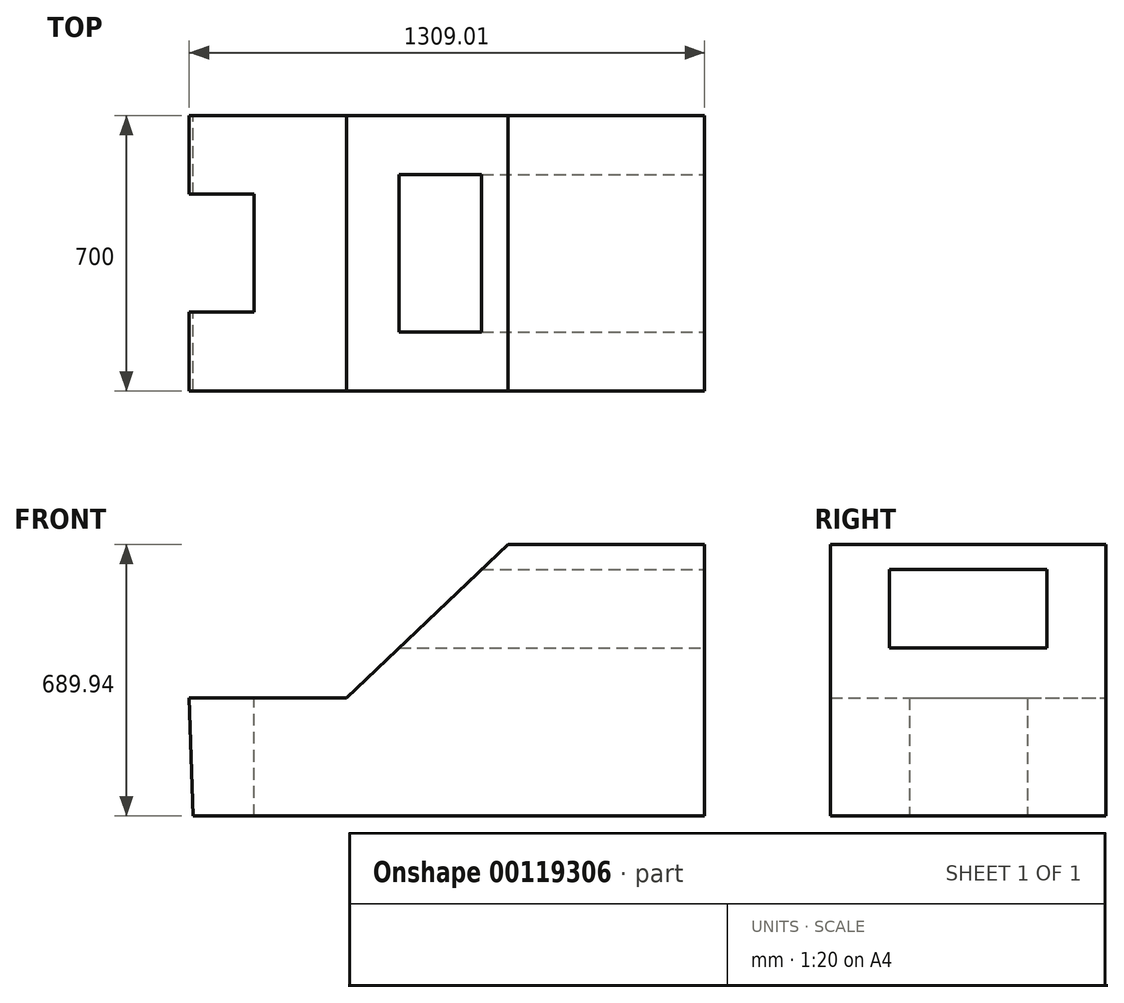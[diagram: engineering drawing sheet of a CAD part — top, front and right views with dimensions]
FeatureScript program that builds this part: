
annotation { "Feature Type Name" : "Feature", "Feature Type Description" : "" }
export const myFeature = defineFeature(function(context is Context, id is Id, definition is map)
    precondition{}
    {
        {
            var Q0;
            Q0=qCreatedBy(makeId("Front.planeOp"),FACE);
            var sketch = newSketch(context, id + "F0", { "sketchPlane" : qUnion([Q0])});
            skLineSegment(sketch, "E0.bottom", {"start": v(-800, -689.94) * mm, "end": v(500, -689.94) * mm});
            skLineSegment(sketch, "E0.left", {"start": v(-800, -689.94) * mm, "end": v(-809, -390.08) * mm});
            skPoint(sketch, "E0.middle", {"position": v(0, 0) * mm});
            skLineSegment(sketch, "E1", {"start": v(-809, -390.08) * mm, "end": v(-409, -390.08) * mm});
            skLineSegment(sketch, "E2", {"start": v(-409, -390.08) * mm, "end": v(0, 0) * mm});
            skLineSegment(sketch, "E3", {"start": v(500, 0) * mm, "end": v(500, -700) * mm});
            skLineSegment(sketch, "E4", {"start": v(-799.7, -700) * mm, "end": v(-800, -689.94) * mm});
            skPoint(sketch, "E5.start.orphan", {"position": v(25.9, 0) * mm});
            skLineSegment(sketch, "E6", {"start": v(0, 0) * mm, "end": v(500, 0) * mm});
            skPoint(sketch, "E7.start.orphan", {"position": v(-841.45, 689.94) * mm});
            skPoint(sketch, "E0.right.end.orphan", {"position": v(800, 689.94) * mm});
            skPoint(sketch, "E8.orphan", {"position": v(841.45, -689.94) * mm});
            skSolve(sketch);
        }
        {
            var Q0;
            Q0 = qSketchRegion(id + "F0", true);
            extrude(context, id + "F1", {"entities" : qUnion([Q0]), "depth" : 700 * mm});
        }
        {
            var Q0;
            Q0=makeQuery(id+"F1.opExtrude","SWEPT_FACE",FACE,{"disambiguationData":[OSD([sQuery(id+"F0.wireOp",EDGE,"E1")])]});
            var sketch = newSketch(context, id + "F2", { "sketchPlane" : qUnion([Q0])});
            skLineSegment(sketch, "E9.top", {"start": v(-644.94, -200) * mm, "end": v(-973.08, -200) * mm});
            skLineSegment(sketch, "E9.left", {"start": v(-644.94, -500) * mm, "end": v(-644.94, -200) * mm});
            skLineSegment(sketch, "E9.right", {"start": v(-973.08, -500) * mm, "end": v(-973.08, -200) * mm});
            skPoint(sketch, "E9.middle", {"position": v(-809, -350) * mm});
            skLineSegment(sketch, "E10", {"start": v(-644.94, -500) * mm, "end": v(-973.08, -500) * mm});
            skSolve(sketch);
        }
        {
            var Q0;
            Q0 = qSketchRegion(id + "F2", true);
            extrude(context, id + "F3", {"entities" : qUnion([Q0]), "operationType" : NewBodyOperationType.REMOVE, "endBound" : BoundingType.THROUGH_ALL, "oppositeDirection" : true, "depth" : 25 * mm});
        }
        {
            var Q0;
            Q0=makeQuery(id+"F1.opExtrude","SWEPT_FACE",FACE,{"disambiguationData":[OSD([sQuery(id+"F0.wireOp",EDGE,"E3")])]});
            var sketch = newSketch(context, id + "F4", { "sketchPlane" : qUnion([Q0])});
            skLineSegment(sketch, "E11.bottom", {"start": v(-150, -63.24) * mm, "end": v(-550, -63.24) * mm});
            skLineSegment(sketch, "E11.top", {"start": v(-150, -263.24) * mm, "end": v(-550, -263.24) * mm});
            skLineSegment(sketch, "E11.left", {"start": v(-150, -63.24) * mm, "end": v(-150, -263.24) * mm});
            skLineSegment(sketch, "E11.right", {"start": v(-550, -63.24) * mm, "end": v(-550, -263.24) * mm});
            skPoint(sketch, "E11.middle", {"position": v(-350, -163.24) * mm});
            skPoint(sketch, "E11.middle.positionSnap0", {"position": v(-350, 0) * mm});
            skPoint(sketch, "E11.centerSnap0", {"position": v(-350, 0) * mm});
            skSolve(sketch);
        }
        {
            var Q0;
            Q0 = qSketchRegion(id + "F4", true);
            extrude(context, id + "F5", {"entities" : qUnion([Q0]), "operationType" : NewBodyOperationType.REMOVE, "endBound" : BoundingType.THROUGH_ALL, "oppositeDirection" : true, "depth" : 25 * mm});
        }
    });
